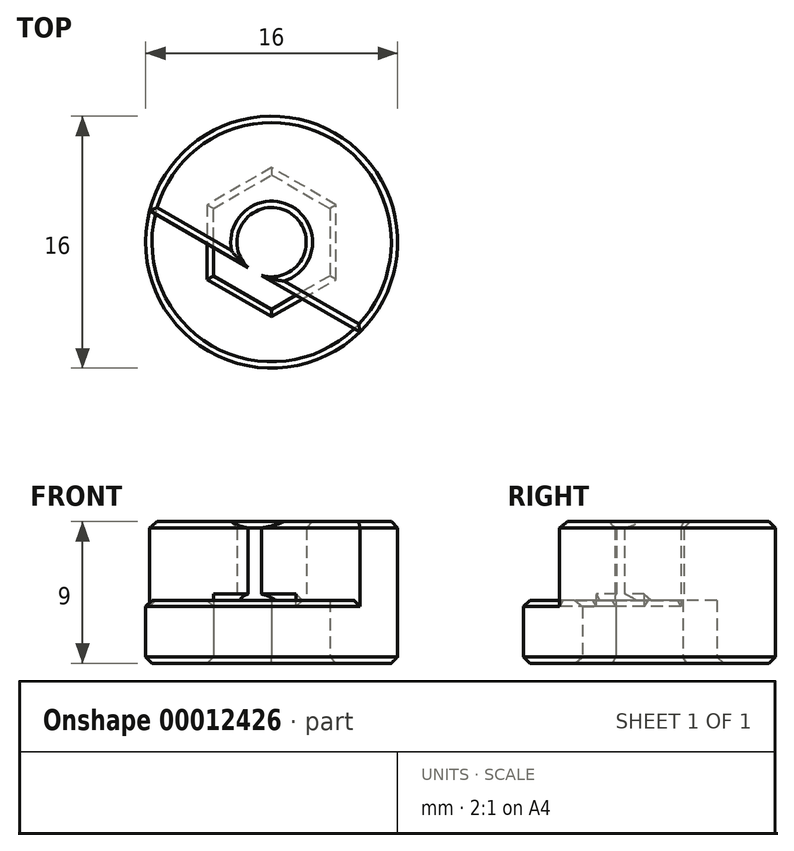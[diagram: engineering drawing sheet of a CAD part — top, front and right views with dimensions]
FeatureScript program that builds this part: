
annotation { "Feature Type Name" : "Feature", "Feature Type Description" : "" }
export const myFeature = defineFeature(function(context is Context, id is Id, definition is map)
    precondition{}
    {
        {
            var Q0;
            Q0=qCreatedBy(makeId("Top.planeOp"),FACE);
            var sketch = newSketch(context, id + "F0", { "sketchPlane" : qUnion([Q0])});
            skCircle(sketch, "E0.cCircle", {"center": v(0, 0) * mm, "radius": 3.7 * mm, "construction": true});
            skLineSegment(sketch, "E0.0", {"start": v(3.7, 2.14) * mm, "end": v(3.7, -2.14) * mm});
            skLineSegment(sketch, "E0.1", {"start": v(3.7, -2.14) * mm, "end": v(0, -4.27) * mm});
            skLineSegment(sketch, "E0.2", {"start": v(0, -4.27) * mm, "end": v(-3.7, -2.14) * mm});
            skLineSegment(sketch, "E0.3", {"start": v(-3.7, -2.14) * mm, "end": v(-3.7, 2.14) * mm});
            skLineSegment(sketch, "E0.4", {"start": v(-3.7, 2.14) * mm, "end": v(0, 4.27) * mm});
            skLineSegment(sketch, "E0.5", {"start": v(0, 4.27) * mm, "end": v(3.7, 2.14) * mm});
            skPoint(sketch, "E0.0.midPoint", {"position": v(3.7, 0) * mm});
            skCircle(sketch, "E1", {"center": v(0, 0) * mm, "radius": 8 * mm});
            skLineSegment(sketch, "E2", {"start": v(1.85, 3.2) * mm, "end": v(4, 6.93) * mm, "construction": true});
            skSolve(sketch);
        }
        {
            var Q0;
            Q0 = qSketchRegion(id + "F0", true);
            extrude(context, id + "F1", {"entities" : qUnion([Q0]), "depth" : 4 * mm});
        }
        {
            var Q0;
            Q0=makeQuery(id+"F1.opExtrude","CAP_FACE",FACE,{"disambiguationData":[OSD([sQuery(id+"F0.wireOp",EDGE,"E0.0"),sQuery(id+"F0.wireOp",EDGE,"E0.1"),sQuery(id+"F0.wireOp",EDGE,"E0.2"),sQuery(id+"F0.wireOp",EDGE,"E0.3"),sQuery(id+"F0.wireOp",EDGE,"E0.4"),sQuery(id+"F0.wireOp",EDGE,"E0.5"),sQuery(id+"F0.wireOp",EDGE,"E1")])],"isStart":false});
            var sketch = newSketch(context, id + "F2", { "sketchPlane" : qUnion([Q0])});
            skArc(sketch, "E3", {"start": v(-0.64, -2.1) * mm, "mid": v(1.1, 1.9) * mm, "end": v(-1.5, -1.6) * mm});
            skArc(sketch, "E4", {"start": v(5.6, -5.7) * mm, "mid": v(4, 6.93) * mm, "end": v(-7.75, 2) * mm});
            skLineSegment(sketch, "E5", {"start": v(-7.75, 2) * mm, "end": v(-1.5, -1.6) * mm});
            skPoint(sketch, "E6", {"position": v(-1.5, -1.6) * mm});
            skPoint(sketch, "E7", {"position": v(-0.64, -2.1) * mm});
            skLineSegment(sketch, "E8.trimOffspring", {"start": v(-0.64, -2.1) * mm, "end": v(5.6, -5.7) * mm});
            skSolve(sketch);
        }
        {
            var Q0;
            Q0 = qSketchRegion(id + "F2", true);
            extrude(context, id + "F3", {"entities" : qUnion([Q0]), "operationType" : NewBodyOperationType.ADD, "depth" : 5 * mm});
        }
        {
            var Q0;
            Q0=makeQuery(id+"F1.opExtrude","CAP_FACE",FACE,{"disambiguationData":[OSD([sQuery(id+"F0.wireOp",EDGE,"E0.0"),sQuery(id+"F0.wireOp",EDGE,"E0.1"),sQuery(id+"F0.wireOp",EDGE,"E0.2"),sQuery(id+"F0.wireOp",EDGE,"E0.3"),sQuery(id+"F0.wireOp",EDGE,"E0.4"),sQuery(id+"F0.wireOp",EDGE,"E0.5"),sQuery(id+"F0.wireOp",EDGE,"E1")])],"isStart":true});
            chamfer(context, id + "F4", {"entities" : qUnion([Q0]), "width" : 0.4 * mm, "tangentPropagation" : true});
        }
        {
            var Q0;
            Q0=makeQuery(id+"F3.opExtrude","CAP_FACE",FACE,{"disambiguationData":[OSD([sQuery(id+"F2.wireOp",EDGE,"E3"),sQuery(id+"F2.wireOp",EDGE,"E4"),sQuery(id+"F2.wireOp",EDGE,"E5"),sQuery(id+"F2.wireOp",EDGE,"E8.trimOffspring")])],"isStart":false});
            chamfer(context, id + "F5", {"entities" : qUnion([Q0]), "width" : 0.4 * mm, "tangentPropagation" : true});
        }
        {
            var Q0;
            {var subQ0=sQuery(id+"F0.wireOp",EDGE,"E0.3");var subQ2=sQuery(id+"F0.wireOp",EDGE,"E0.2");Q0=makeQuery(id+"F3.boolean.opBoolean","SPLIT",EDGE,{"disambiguationData":[TD([makeQuery(id+"F1.opExtrude","SWEPT_FACE",FACE,{"disambiguationData":[OSD([subQ2])]})])],"derivedFrom":makeQuery(id+"F1.opExtrude","CAP_EDGE",EDGE,{"disambiguationData":[OSD([subQ0])],"isStart":false})});}
            var Q1;
            Q1=makeQuery(id+"F1.opExtrude","CAP_EDGE",EDGE,{"disambiguationData":[OSD([sQuery(id+"F0.wireOp",EDGE,"E0.2")])],"isStart":false});
            var Q2;
            {var subQ0=sQuery(id+"F0.wireOp",EDGE,"E0.1");var subQ2=sQuery(id+"F0.wireOp",EDGE,"E0.2");Q2=makeQuery(id+"F3.boolean.opBoolean","SPLIT",EDGE,{"disambiguationData":[TD([makeQuery(id+"F1.opExtrude","SWEPT_FACE",FACE,{"disambiguationData":[OSD([subQ2])]})])],"derivedFrom":makeQuery(id+"F1.opExtrude","CAP_EDGE",EDGE,{"disambiguationData":[OSD([subQ0])],"isStart":false})});}
            var Q3;
            Q3=makeQuery(id+"F1.opExtrude","CAP_EDGE",EDGE,{"disambiguationData":[OSD([sQuery(id+"F0.wireOp",EDGE,"E1")])],"isStart":false});
            chamfer(context, id + "F6", {"entities" : qUnion([Q0, Q1, Q2, Q3]), "width" : 0.4 * mm, "tangentPropagation" : true});
        }
        {
            var Q0;
            {var subQ0=sQuery(id+"F2.wireOp",EDGE,"E5");var subQ2=sQuery(id+"F0.wireOp",EDGE,"E1");Q0=makeQuery(id+"F3.boolean.opBoolean","SPLIT",EDGE,{"disambiguationData":[TD([makeQuery(id+"F1.opExtrude","SWEPT_FACE",FACE,{"disambiguationData":[OSD([subQ2])]})])],"derivedFrom":makeQuery(id+"F3.opExtrude","CAP_EDGE",EDGE,{"disambiguationData":[OSD([subQ0])],"isStart":true})});}
            var Q1;
            {var subQ0=sQuery(id+"F2.wireOp",EDGE,"E8.trimOffspring");var subQ2=sQuery(id+"F0.wireOp",EDGE,"E1");Q1=makeQuery(id+"F3.boolean.opBoolean","SPLIT",EDGE,{"disambiguationData":[TD([makeQuery(id+"F1.opExtrude","SWEPT_FACE",FACE,{"disambiguationData":[OSD([subQ2])]})])],"derivedFrom":makeQuery(id+"F3.opExtrude","CAP_EDGE",EDGE,{"disambiguationData":[OSD([subQ0])],"isStart":true})});}
            chamfer(context, id + "F7", {"entities" : qUnion([Q0, Q1]), "width" : 0.4 * mm, "tangentPropagation" : true});
        }
    });
